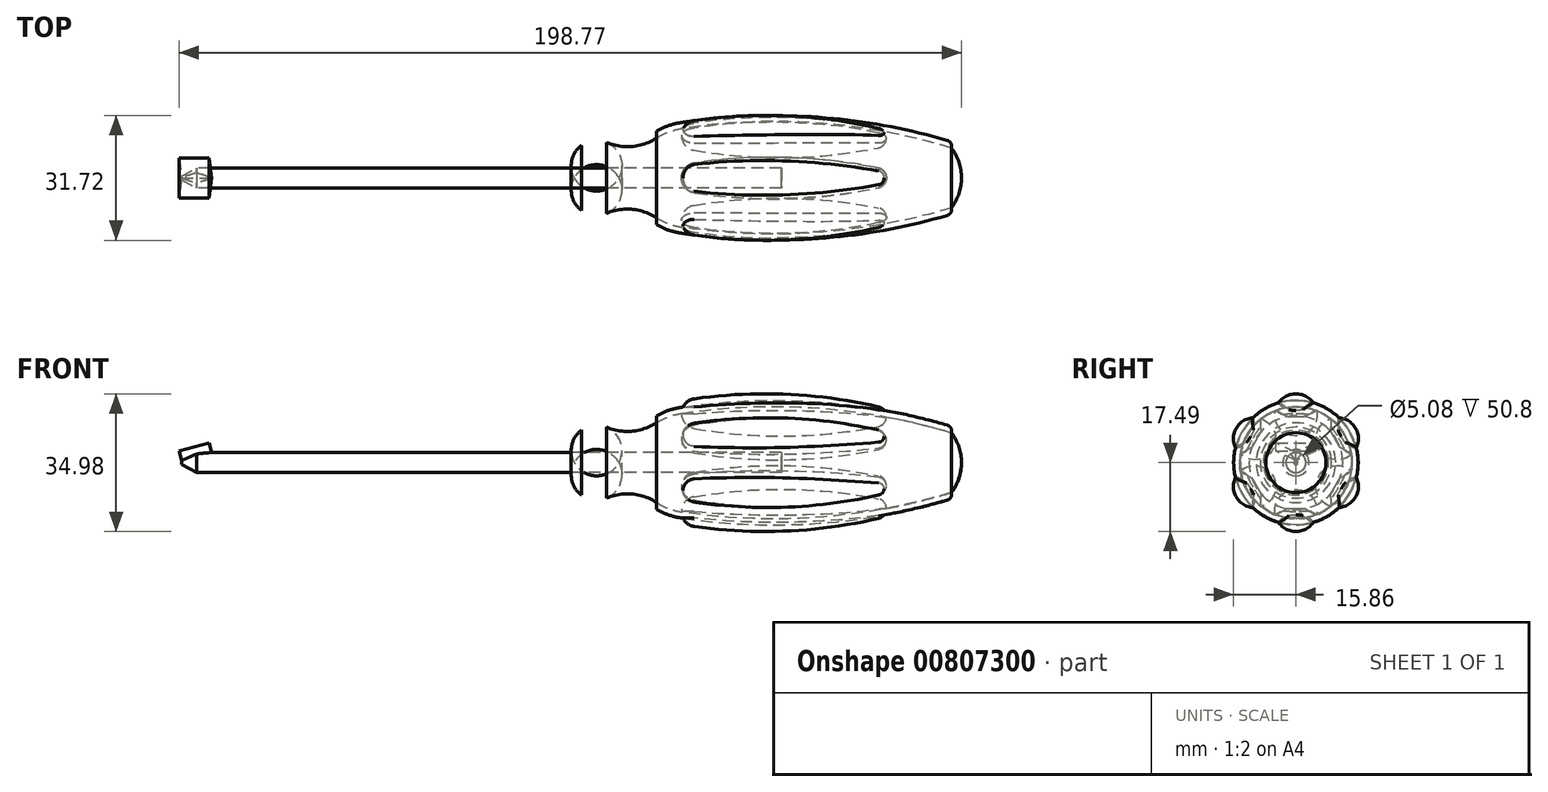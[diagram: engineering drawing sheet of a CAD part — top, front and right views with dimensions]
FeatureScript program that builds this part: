
annotation { "Feature Type Name" : "Feature", "Feature Type Description" : "" }
export const myFeature = defineFeature(function(context is Context, id is Id, definition is map)
    precondition{}
    {
        {
            var Q0;
            Q0=qCreatedBy(makeId("Front.planeOp"),FACE);
            var sketch = newSketch(context, id + "F0", { "sketchPlane" : qUnion([Q0])});
            skLineSegment(sketch, "E0", {"start": v(-101.6, 0) * mm, "end": v(96.52, 0) * mm});
            skLineSegment(sketch, "E1", {"start": v(96.52, 0) * mm, "end": v(117.55, 0) * mm, "construction": true});
            skLineSegment(sketch, "E2", {"start": v(50.8, 2.54) * mm, "end": v(-97.8, 2.54) * mm});
            skLineSegment(sketch, "E3", {"start": v(-101.6, 0.5) * mm, "end": v(-101.6, 0) * mm});
            skLineSegment(sketch, "E4", {"start": v(0, 2.54) * mm, "end": v(0, 8.25) * mm});
            skArc(sketch, "E5", {"start": v(6.35, 9.02) * mm, "mid": v(3.07, 9.48) * mm, "end": v(0, 8.25) * mm});
            skArc(sketch, "E6", {"start": v(6.35, 9.02) * mm, "mid": v(12.84, 7.99) * mm, "end": v(19.05, 10.11) * mm});
            skArc(sketch, "E7", {"start": v(25.4, 12.52) * mm, "mid": v(22.1, 11.65) * mm, "end": v(19.05, 10.11) * mm});
            skArc(sketch, "E8", {"start": v(93.98, 7.62) * mm, "mid": v(59.96, 13.9) * mm, "end": v(25.4, 12.52) * mm});
            skArc(sketch, "E9", {"start": v(96.52, 0) * mm, "mid": v(95.87, 4.02) * mm, "end": v(93.98, 7.62) * mm});
            skArc(sketch, "E10.0", {"start": v(25.17, 14.02) * mm, "mid": v(22.01, 13.24) * mm, "end": v(19.05, 11.9) * mm});
            skArc(sketch, "E10.1", {"start": v(92.95, 9.52) * mm, "mid": v(59.3, 15.46) * mm, "end": v(25.17, 14.02) * mm});
            skLineSegment(sketch, "E11", {"start": v(19.05, 11.9) * mm, "end": v(19.05, 10.11) * mm});
            skArc(sketch, "E12", {"start": v(93.98, 7.62) * mm, "mid": v(93.86, 8.78) * mm, "end": v(92.95, 9.52) * mm});
            skPoint(sketch, "E13.orphan", {"position": v(0, 0) * mm});
            skLineSegment(sketch, "E14", {"start": v(50.8, 2.54) * mm, "end": v(50.8, 0) * mm});
            skLineSegment(sketch, "E15", {"start": v(-101.6, 0.5) * mm, "end": v(-97.8, 2.54) * mm});
            skPoint(sketch, "E16.orphan", {"position": v(-101.6, 2.54) * mm});
            skSolve(sketch);
        }
        {
            var Q0;
            Q0=qCreatedBy(makeId("Front.planeOp"),FACE);
            var sketch = newSketch(context, id + "F1", { "sketchPlane" : qUnion([Q0])});
            skLineSegment(sketch, "E17", {"start": v(25.4, 12.52) * mm, "end": v(77.47, 11.64) * mm});
            skArc(sketch, "E18", {"start": v(28.67, 16.22) * mm, "mid": v(26.35, 14.97) * mm, "end": v(25.4, 12.52) * mm});
            skArc(sketch, "E19", {"start": v(77.47, 11.64) * mm, "mid": v(76.93, 13.25) * mm, "end": v(75.5, 14.16) * mm});
            skArc(sketch, "E20", {"start": v(75.5, 14.16) * mm, "mid": v(52.19, 17.37) * mm, "end": v(28.67, 16.22) * mm});
            skSolve(sketch);
        }
        {
            var Q0;
            Q0=qCreatedBy(makeId("Front.planeOp"),FACE);
            var sketch = newSketch(context, id + "F2", { "sketchPlane" : qUnion([Q0])});
            skLineSegment(sketch, "E21", {"start": v(-101.6, 0.5) * mm, "end": v(-93.98, 2.54) * mm});
            skSolve(sketch);
        }
        {
            var Q0;
            Q0=sQuery(id+"F2.wireOp",VERTEX,"E21.start");
            var Q1;
            Q1=sQuery(id+"F2.wireOp",EDGE,"E21");
            cPlane(context, id + "F3", {"entities" : qUnion([Q0, Q1]), "cplaneType" : CPlaneType.LINE_POINT, "offset" : 25.4 * mm, "width" : 152.4 * mm, "height" : 152.4 * mm});
        }
        {
            var Q0;
            Q0=qCreatedBy(id+"F3.planeOp",FACE);
            var sketch = newSketch(context, id + "F4", { "sketchPlane" : qUnion([Q0])});
            skLineSegment(sketch, "E22", {"start": v(5.08, 29.2) * mm, "end": v(0, 26.67) * mm});
            skLineSegment(sketch, "E23", {"start": v(0, 26.67) * mm, "end": v(-5.08, 29.2) * mm});
            skLineSegment(sketch, "E24", {"start": v(-5.08, 29.2) * mm, "end": v(5.08, 29.2) * mm});
            skLineSegment(sketch, "E25", {"start": v(0, 29.2) * mm, "end": v(0, 26.67) * mm, "construction": true});
            skSolve(sketch);
        }
        {
            var Q0;
            {var subQ0=sQuery(id+"F0.wireOp",EDGE,"E3");Q0=makeQuery(id+"F0.imprint","IMPRINT",FACE,{"disambiguationData":[TD([[makeQuery(id+"F0.imprint","IMPRINT",EDGE,{"derivedFrom":subQ0}),1.0]])]});}
            var Q1;
            Q1=sQuery(id+"F0.wireOp",EDGE,"E1");
            revolve(context, id + "F5", {"surfaceOperationType" : NewSurfaceOperationType.NEW, "entities" : qUnion([Q0]), "axis" : qUnion([Q1]), "revolveType" : RevolveType.FULL});
        }
        {
            var Q0;
            Q0=makeQuery(id+"F1.imprint","IMPRINT",FACE,{"disambiguationData":[TD([[makeQuery(id+"F1.imprint","IMPRINT",EDGE,{"derivedFrom":sQuery(id+"F1.wireOp",EDGE,"E17")}),1.0]])]});
            var Q1;
            Q1=sQuery(id+"F1.wireOp",EDGE,"E17");
            revolve(context, id + "F6", {"operationType" : NewBodyOperationType.ADD, "surfaceOperationType" : NewSurfaceOperationType.NEW, "entities" : qUnion([Q0]), "axis" : qUnion([Q1]), "revolveType" : RevolveType.FULL});
        }
        {
            var Q0;
            Q0=makeQuery(id+"F5.opRevolve","SWEPT_BODY",BODY,{"disambiguationData":[OSD([sQuery(id+"F0.wireOp",EDGE,"E0"),sQuery(id+"F0.wireOp",EDGE,"E2"),sQuery(id+"F0.wireOp",EDGE,"E3"),sQuery(id+"F0.wireOp",EDGE,"E4"),sQuery(id+"F0.wireOp",EDGE,"E5"),sQuery(id+"F0.wireOp",EDGE,"E6"),sQuery(id+"F0.wireOp",EDGE,"E9"),sQuery(id+"F0.wireOp",EDGE,"E10.0"),sQuery(id+"F0.wireOp",EDGE,"E10.1"),sQuery(id+"F0.wireOp",EDGE,"E11"),sQuery(id+"F0.wireOp",EDGE,"E12"),sQuery(id+"F0.wireOp",EDGE,"E15")])]});
            var Q1;
            Q1=sQuery(id+"F0.wireOp",EDGE,"E1");
            circularPattern(context, id + "F7", {"entities" : qUnion([Q0]), "axis" : qUnion([Q1]), "angle" : 360 * degree, "instanceCount" : 6, "equalSpace" : true});
        }
        {
            var Q0;
            Q0=makeQuery(id+"F0.imprint","IMPRINT",FACE,{"disambiguationData":[TD([[makeQuery(id+"F0.imprint","IMPRINT",EDGE,{"derivedFrom":sQuery(id+"F0.wireOp",EDGE,"E7")}),-1.0]])]});
            var Q1;
            Q1=sQuery(id+"F0.wireOp",EDGE,"E1");
            revolve(context, id + "F8", {"operationType" : NewBodyOperationType.ADD, "surfaceOperationType" : NewSurfaceOperationType.NEW, "entities" : qUnion([Q0]), "axis" : qUnion([Q1]), "revolveType" : RevolveType.FULL});
        }
        {
            var Q0;
            {var subQ0=sQuery(id+"F0.wireOp",EDGE,"E4");Q0=makeQuery(id+"F0.imprint","IMPRINT",FACE,{"disambiguationData":[TD([[makeQuery(id+"F0.imprint","IMPRINT",EDGE,{"derivedFrom":subQ0}),-1.0]])]});}
            var Q1;
            Q1=sQuery(id+"F0.wireOp",EDGE,"E1");
            revolve(context, id + "F9", {"surfaceOperationType" : NewSurfaceOperationType.NEW, "entities" : qUnion([Q0]), "axis" : qUnion([Q1]), "revolveType" : RevolveType.FULL});
        }
        {
            var Q0;
            Q0=makeQuery(id+"F6.opRevolve","SWEPT_BODY",BODY,{"disambiguationData":[OSD([sQuery(id+"F1.wireOp",EDGE,"E17"),sQuery(id+"F1.wireOp",EDGE,"E18"),sQuery(id+"F1.wireOp",EDGE,"E19"),sQuery(id+"F1.wireOp",EDGE,"E20")])]});
            var Q1;
            Q1=sQuery(id+"F0.wireOp",EDGE,"E1");
            circularPattern(context, id + "F10", {"entities" : qUnion([Q0]), "axis" : qUnion([Q1]), "angle" : 360 * degree, "instanceCount" : 6, "equalSpace" : true});
        }
        {
            var Q0;
            Q0=makeQuery(id+"F4.imprint","IMPRINT",FACE,{"disambiguationData":[TD([[makeQuery(id+"F4.imprint","IMPRINT",EDGE,{"derivedFrom":sQuery(id+"F4.wireOp",EDGE,"E22")}),-1.0]])]});
            var Q1;
            Q1=sQuery(id+"F2.wireOp",EDGE,"E21");
            sweep(context, id + "F11", {"operationType" : NewBodyOperationType.REMOVE, "profiles" : qUnion([Q0]), "path" : qUnion([Q1])});
        }
        {
            var Q0;
            Q0=makeQuery(id+"F4.imprint","IMPRINT",FACE,{"disambiguationData":[TD([[makeQuery(id+"F4.imprint","IMPRINT",EDGE,{"derivedFrom":sQuery(id+"F4.wireOp",EDGE,"E22")}),-1.0]])]});
            var Q1;
            Q1=sQuery(id+"F0.wireOp",EDGE,"E15");
            sweep(context, id + "F12", {"operationType" : NewBodyOperationType.REMOVE, "profiles" : qUnion([Q0]), "path" : qUnion([Q1])});
        }
        {
            var Q0;
            Q0=makeQuery(id+"F4.imprint","IMPRINT",FACE,{"disambiguationData":[TD([[makeQuery(id+"F4.imprint","IMPRINT",EDGE,{"derivedFrom":sQuery(id+"F4.wireOp",EDGE,"E22")}),-1.0]])]});
            var Q1;
            Q1=sQuery(id+"F0.wireOp",EDGE,"E15");
            sweep(context, id + "F13", {"operationType" : NewBodyOperationType.REMOVE, "profiles" : qUnion([Q0]), "path" : qUnion([Q1])});
        }
        {
            var Q0;
            Q0=makeQuery(id+"F4.imprint","IMPRINT",FACE,{"disambiguationData":[TD([[makeQuery(id+"F4.imprint","IMPRINT",EDGE,{"derivedFrom":sQuery(id+"F4.wireOp",EDGE,"E22")}),-1.0]])]});
            var Q1;
            Q1=sQuery(id+"F0.wireOp",EDGE,"E15");
            sweep(context, id + "F14", {"operationType" : NewBodyOperationType.REMOVE, "profiles" : qUnion([Q0]), "path" : qUnion([Q1])});
        }
        {
            var Q0;
            Q0=makeQuery(id+"F4.imprint","IMPRINT",FACE,{"disambiguationData":[TD([[makeQuery(id+"F4.imprint","IMPRINT",EDGE,{"derivedFrom":sQuery(id+"F4.wireOp",EDGE,"E22")}),-1.0]])]});
            var Q1;
            Q1=sQuery(id+"F2.wireOp",EDGE,"E21");
            sweep(context, id + "F15", {"operationType" : NewBodyOperationType.REMOVE, "profiles" : qUnion([Q0]), "path" : qUnion([Q1])});
        }
        {
            var Q0;
            Q0=makeQuery(id+"F4.imprint","IMPRINT",FACE,{"disambiguationData":[TD([[makeQuery(id+"F4.imprint","IMPRINT",EDGE,{"derivedFrom":sQuery(id+"F4.wireOp",EDGE,"E22")}),-1.0]])]});
            var Q1;
            Q1=sQuery(id+"F2.wireOp",EDGE,"E21");
            sweep(context, id + "F16", {"operationType" : NewBodyOperationType.REMOVE, "profiles" : qUnion([Q0]), "path" : qUnion([Q1])});
        }
        {
            var Q0;
            Q0=makeQuery(id+"F4.imprint","IMPRINT",FACE,{"disambiguationData":[TD([[makeQuery(id+"F4.imprint","IMPRINT",EDGE,{"derivedFrom":sQuery(id+"F4.wireOp",EDGE,"E22")}),-1.0]])]});
            var Q1;
            Q1=qConstructionFilter(qBodyType(qCreatedBy(id+"F2",EDGE),BodyType.WIRE),ConstructionObject.NO);
            sweep(context, id + "F17", {"profiles" : qUnion([Q0]), "path" : qUnion([Q1])});
        }
    });
